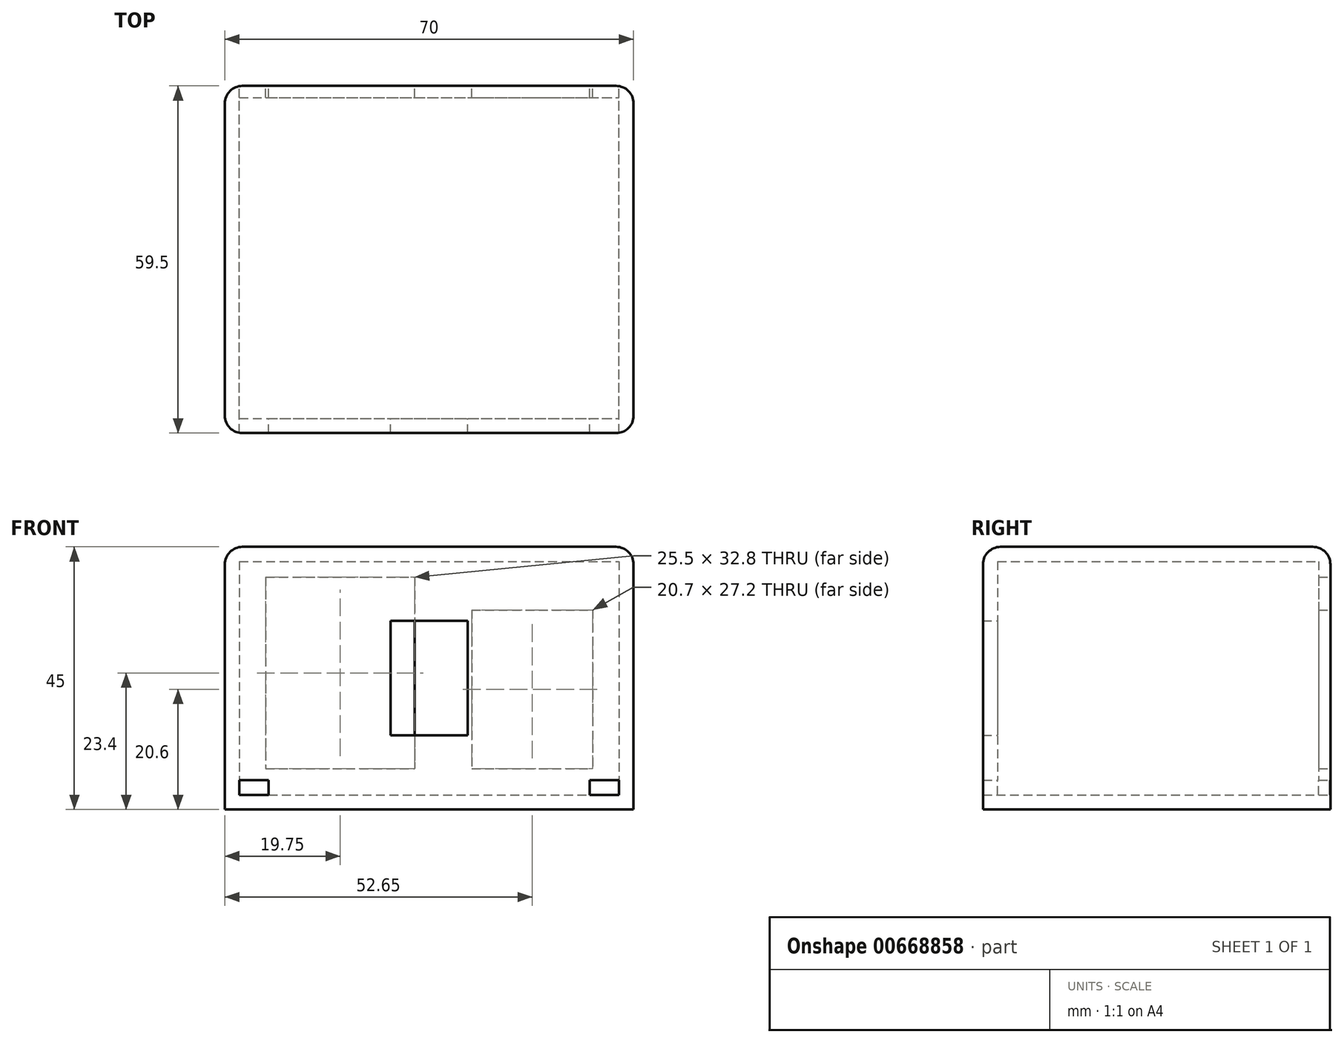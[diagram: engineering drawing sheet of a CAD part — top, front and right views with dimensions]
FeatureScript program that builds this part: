
annotation { "Feature Type Name" : "Feature", "Feature Type Description" : "" }
export const myFeature = defineFeature(function(context is Context, id is Id, definition is map)
    precondition{}
    {
        {
            var Q0;
            Q0=qCreatedBy(makeId("Front.planeOp"),FACE);
            var sketch = newSketch(context, id + "F0", { "sketchPlane" : qUnion([Q0])});
            skLineSegment(sketch, "E0.bottom", {"start": v(-35, 22.5) * mm, "end": v(35, 22.5) * mm});
            skLineSegment(sketch, "E0.top", {"start": v(-35, -22.5) * mm, "end": v(35, -22.5) * mm});
            skLineSegment(sketch, "E0.left", {"start": v(-35, 22.5) * mm, "end": v(-35, -22.5) * mm});
            skLineSegment(sketch, "E0.right", {"start": v(35, 22.5) * mm, "end": v(35, -22.5) * mm});
            skLineSegment(sketch, "E1.bottom", {"start": v(-28, 17.3) * mm, "end": v(-2.5, 17.3) * mm});
            skLineSegment(sketch, "E1.top", {"start": v(-28, -15.5) * mm, "end": v(-2.5, -15.5) * mm});
            skLineSegment(sketch, "E1.left", {"start": v(-28, 17.3) * mm, "end": v(-28, -15.5) * mm});
            skLineSegment(sketch, "E1.right", {"start": v(-2.5, 17.3) * mm, "end": v(-2.5, -15.5) * mm});
            skLineSegment(sketch, "E2.bottom", {"start": v(7.3, 11.7) * mm, "end": v(28, 11.7) * mm});
            skLineSegment(sketch, "E2.top", {"start": v(7.3, -15.5) * mm, "end": v(28, -15.5) * mm});
            skLineSegment(sketch, "E2.left", {"start": v(7.3, 11.7) * mm, "end": v(7.3, -15.5) * mm});
            skLineSegment(sketch, "E2.right", {"start": v(28, 11.7) * mm, "end": v(28, -15.5) * mm});
            skSolve(sketch);
        }
        {
            var Q0;
            Q0 = qSketchRegion(id + "F0", true);
            extrude(context, id + "F1", {"entities" : qUnion([Q0]), "depth" : 2 * mm, "offsetDistance" : 25 * mm});
        }
        {
            var Q0;
            Q0=makeQuery(id+"F1.opExtrude","CAP_FACE",FACE,{"disambiguationData":[OSD([sQuery(id+"F0.wireOp",EDGE,"E0.bottom"),sQuery(id+"F0.wireOp",EDGE,"E0.top"),sQuery(id+"F0.wireOp",EDGE,"E0.left"),sQuery(id+"F0.wireOp",EDGE,"E0.right"),sQuery(id+"F0.wireOp",EDGE,"E1.bottom"),sQuery(id+"F0.wireOp",EDGE,"E1.top"),sQuery(id+"F0.wireOp",EDGE,"E1.left"),sQuery(id+"F0.wireOp",EDGE,"E1.right"),sQuery(id+"F0.wireOp",EDGE,"E2.bottom"),sQuery(id+"F0.wireOp",EDGE,"E2.top"),sQuery(id+"F0.wireOp",EDGE,"E2.left"),sQuery(id+"F0.wireOp",EDGE,"E2.right")])],"isStart":false});
            var sketch = newSketch(context, id + "F2", { "sketchPlane" : qUnion([Q0])});
            skLineSegment(sketch, "E3.0", {"start": v(-35, 22.5) * mm, "end": v(35, 22.5) * mm});
            skLineSegment(sketch, "E4.0", {"start": v(-35, 22.5) * mm, "end": v(-35, -22.5) * mm});
            skLineSegment(sketch, "E5.0", {"start": v(-35, -22.5) * mm, "end": v(35, -22.5) * mm});
            skLineSegment(sketch, "E6.0", {"start": v(35, 22.5) * mm, "end": v(35, -22.5) * mm});
            skLineSegment(sketch, "E7.bottom", {"start": v(-32.5, 20) * mm, "end": v(32.5, 20) * mm});
            skLineSegment(sketch, "E7.top", {"start": v(-32.5, -20) * mm, "end": v(32.5, -20) * mm});
            skLineSegment(sketch, "E7.left", {"start": v(-32.5, 20) * mm, "end": v(-32.5, -20) * mm});
            skLineSegment(sketch, "E7.right", {"start": v(32.5, 20) * mm, "end": v(32.5, -20) * mm});
            skSolve(sketch);
        }
        {
            var Q0;
            Q0 = qSketchRegion(id + "F2", true);
            extrude(context, id + "F3", {"entities" : qUnion([Q0]), "operationType" : NewBodyOperationType.ADD, "depth" : 55 * mm, "offsetDistance" : 25 * mm});
        }
        {
            var Q0;
            Q0=makeQuery(id+"F3.opExtrude","CAP_FACE",FACE,{"disambiguationData":[OSD([sQuery(id+"F2.wireOp",EDGE,"E3.0"),sQuery(id+"F2.wireOp",EDGE,"E4.0"),sQuery(id+"F2.wireOp",EDGE,"E5.0"),sQuery(id+"F2.wireOp",EDGE,"E6.0"),sQuery(id+"F2.wireOp",EDGE,"E7.bottom"),sQuery(id+"F2.wireOp",EDGE,"E7.top"),sQuery(id+"F2.wireOp",EDGE,"E7.left"),sQuery(id+"F2.wireOp",EDGE,"E7.right")])],"isStart":false});
            var sketch = newSketch(context, id + "F4", { "sketchPlane" : qUnion([Q0])});
            skLineSegment(sketch, "E8.0", {"start": v(-35, 22.5) * mm, "end": v(35, 22.5) * mm});
            skLineSegment(sketch, "E9.0", {"start": v(-35, 22.5) * mm, "end": v(-35, -22.5) * mm});
            skLineSegment(sketch, "E10.0", {"start": v(-35, -22.5) * mm, "end": v(35, -22.5) * mm});
            skLineSegment(sketch, "E11.0", {"start": v(35, 22.5) * mm, "end": v(35, -22.5) * mm});
            skLineSegment(sketch, "E12.bottom", {"start": v(-6.6, 9.8) * mm, "end": v(6.6, 9.8) * mm});
            skLineSegment(sketch, "E12.top", {"start": v(-6.6, -9.8) * mm, "end": v(6.6, -9.8) * mm});
            skLineSegment(sketch, "E12.left", {"start": v(-6.6, 9.8) * mm, "end": v(-6.6, -9.8) * mm});
            skLineSegment(sketch, "E12.right", {"start": v(6.6, 9.8) * mm, "end": v(6.6, -9.8) * mm});
            skSolve(sketch);
        }
        {
            var Q0;
            Q0 = qSketchRegion(id + "F4", true);
            extrude(context, id + "F5", {"entities" : qUnion([Q0]), "operationType" : NewBodyOperationType.ADD, "depth" : 2.5 * mm, "offsetDistance" : 25 * mm});
        }
        {
            var Q0;
            Q0=makeQuery(id+"F1.opExtrude","CAP_FACE",FACE,{"disambiguationData":[OSD([sQuery(id+"F0.wireOp",EDGE,"E0.bottom"),sQuery(id+"F0.wireOp",EDGE,"E0.top"),sQuery(id+"F0.wireOp",EDGE,"E0.left"),sQuery(id+"F0.wireOp",EDGE,"E0.right"),sQuery(id+"F0.wireOp",EDGE,"E1.bottom"),sQuery(id+"F0.wireOp",EDGE,"E1.top"),sQuery(id+"F0.wireOp",EDGE,"E1.left"),sQuery(id+"F0.wireOp",EDGE,"E1.right"),sQuery(id+"F0.wireOp",EDGE,"E2.bottom"),sQuery(id+"F0.wireOp",EDGE,"E2.top"),sQuery(id+"F0.wireOp",EDGE,"E2.left"),sQuery(id+"F0.wireOp",EDGE,"E2.right")])],"isStart":true});
            var sketch = newSketch(context, id + "F6", { "sketchPlane" : qUnion([Q0])});
            skPoint(sketch, "E13.0", {"position": v(-35, -22.5) * mm});
            skPoint(sketch, "E14.0", {"position": v(35, -22.5) * mm});
            skLineSegment(sketch, "E15.bottom", {"start": v(-32.5, -17.5) * mm, "end": v(-27.5, -17.5) * mm});
            skLineSegment(sketch, "E15.top", {"start": v(-32.5, -20) * mm, "end": v(-27.5, -20) * mm});
            skLineSegment(sketch, "E15.left", {"start": v(-32.5, -17.5) * mm, "end": v(-32.5, -20) * mm});
            skLineSegment(sketch, "E15.right", {"start": v(-27.5, -17.5) * mm, "end": v(-27.5, -20) * mm});
            skLineSegment(sketch, "E16.bottom", {"start": v(27.5, -20) * mm, "end": v(32.5, -20) * mm});
            skLineSegment(sketch, "E16.top", {"start": v(27.5, -17.5) * mm, "end": v(32.5, -17.5) * mm});
            skLineSegment(sketch, "E16.left", {"start": v(27.5, -20) * mm, "end": v(27.5, -17.5) * mm});
            skLineSegment(sketch, "E16.right", {"start": v(32.5, -20) * mm, "end": v(32.5, -17.5) * mm});
            skSolve(sketch);
        }
        {
            var Q0;
            Q0=makeQuery(id+"F6.imprint","IMPRINT",FACE,{"disambiguationData":[TD([[makeQuery(id+"F6.imprint","IMPRINT",EDGE,{"derivedFrom":sQuery(id+"F6.wireOp",EDGE,"E15.bottom")}),-1.0]])]});
            var Q1;
            Q1=makeQuery(id+"F6.imprint","IMPRINT",FACE,{"disambiguationData":[TD([[makeQuery(id+"F6.imprint","IMPRINT",EDGE,{"derivedFrom":sQuery(id+"F6.wireOp",EDGE,"E16.bottom")}),1.0]])]});
            extrude(context, id + "F7", {"entities" : qUnion([Q0, Q1]), "operationType" : NewBodyOperationType.REMOVE, "endBound" : BoundingType.THROUGH_ALL, "oppositeDirection" : true, "depth" : 25 * mm, "offsetDistance" : 25 * mm});
        }
        {
            var Q0;
            Q0=makeQuery(id+"F5.opExtrude","CAP_EDGE",EDGE,{"disambiguationData":[OSD([sQuery(id+"F4.wireOp",EDGE,"E8.0")])],"isStart":false});
            var Q1;
            Q1=makeQuery(id+"F5.opExtrude","CAP_EDGE",EDGE,{"disambiguationData":[OSD([sQuery(id+"F4.wireOp",EDGE,"E11.0")])],"isStart":false});
            var Q2;
            Q2=makeQuery(id+"F5.opExtrude","CAP_EDGE",EDGE,{"disambiguationData":[OSD([sQuery(id+"F4.wireOp",EDGE,"E9.0")])],"isStart":false});
            var Q3;
            Q3=makeQuery(id+"F5.boolean.opBoolean","MERGE",FACE,{"derivedFrom":[makeQuery(id+"F3.boolean.opBoolean","MERGE",FACE,{"derivedFrom":[makeQuery(id+"F1.opExtrude","SWEPT_FACE",FACE,{"disambiguationData":[OSD([sQuery(id+"F0.wireOp",EDGE,"E0.bottom")])]}),makeQuery(id+"F3.opExtrude","SWEPT_FACE",FACE,{"disambiguationData":[OSD([sQuery(id+"F2.wireOp",EDGE,"E3.0")])]})]}),makeQuery(id+"F5.opExtrude","SWEPT_FACE",FACE,{"disambiguationData":[OSD([sQuery(id+"F4.wireOp",EDGE,"E8.0")])]})]});
            var Q4;
            Q4=makeQuery(id+"F1.opExtrude","CAP_EDGE",EDGE,{"disambiguationData":[OSD([sQuery(id+"F0.wireOp",EDGE,"E0.right")])],"isStart":true});
            var Q5;
            Q5=makeQuery(id+"F1.opExtrude","CAP_EDGE",EDGE,{"disambiguationData":[OSD([sQuery(id+"F0.wireOp",EDGE,"E0.left")])],"isStart":true});
            fillet(context, id + "F8", {"entities" : qUnion([Q0, Q1, Q2, Q3, Q4, Q5]), "radius" : 3 * mm, "tangentPropagation" : true, "allowEdgeOverflow" : false});
        }
    });
